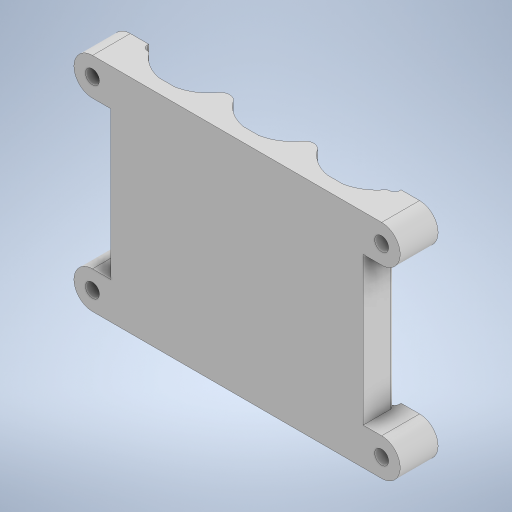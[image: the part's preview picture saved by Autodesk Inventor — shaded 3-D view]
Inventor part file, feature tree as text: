
AUTODESK INVENTOR PART (.ipt)
format: ipt  version: 2023.1 (Build 271208000, 208)  size: 325,120 bytes
history: native  units: mm
features: projected_geometry x4, extrude x3, fillet x3, sketch x3, other x1
ambient origin geometry x8: Origin, YZ Plane, XZ Plane, XY Plane, X Axis, Y Axis, Z Axis, Center Point
bodies: Body1 (feature_tree)
feature tree (14):
  other  "솔리드1"
  extrude  "돌출1"  Depth=62.6mm
  extrude  "돌출2"  Depth=40.0mm
  fillet  "모깎기1"  Radius=3.0mm
  fillet  "모깎기2"  Radius=3.0mm
  extrude  "돌출3"  Depth=3.0mm
  fillet  "모깎기3"  Radius=3.0mm
  sketch  "스케치1"
  sketch  "스케치2"
  sketch  "스케치3"
  projected_geometry  "투영된 루프1"
  projected_geometry  "투영된 루프2"
  projected_geometry  "투영된 루프3"
  projected_geometry  "투영된 루프4"
